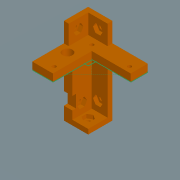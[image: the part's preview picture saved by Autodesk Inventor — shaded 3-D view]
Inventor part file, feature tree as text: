
AUTODESK INVENTOR PART (.ipt)
format: ipt  version: 2016 (Build 200138000, 138)  size: 174,592 bytes
history: native  units: mm (DEFAULTED — no unit token found)
features: sketch x10, other x3
ambient origin geometry x8: Origin, YZ Plane, XZ Plane, XY Plane, X Axis, Y Axis, Z Axis, Center Point
bodies: Solid1 (feature_tree)
feature tree (13):
  other  "MotorMountLeft.ipt"
  other  "Solid1::MotorMountLeft.ipt"
  other  "TaggingFeature1"
  sketch  "Sketch1"  dims[d0=10.0mm]
  sketch  "Sketch2"
  sketch  "Sketch3"
  sketch  "Sketch4"
  sketch  "Sketch5"
  sketch  "Sketch6"
  sketch  "Sketch7"
  sketch  "Sketch8"
  sketch  "Sketch9"
  sketch  "Sketch11"
